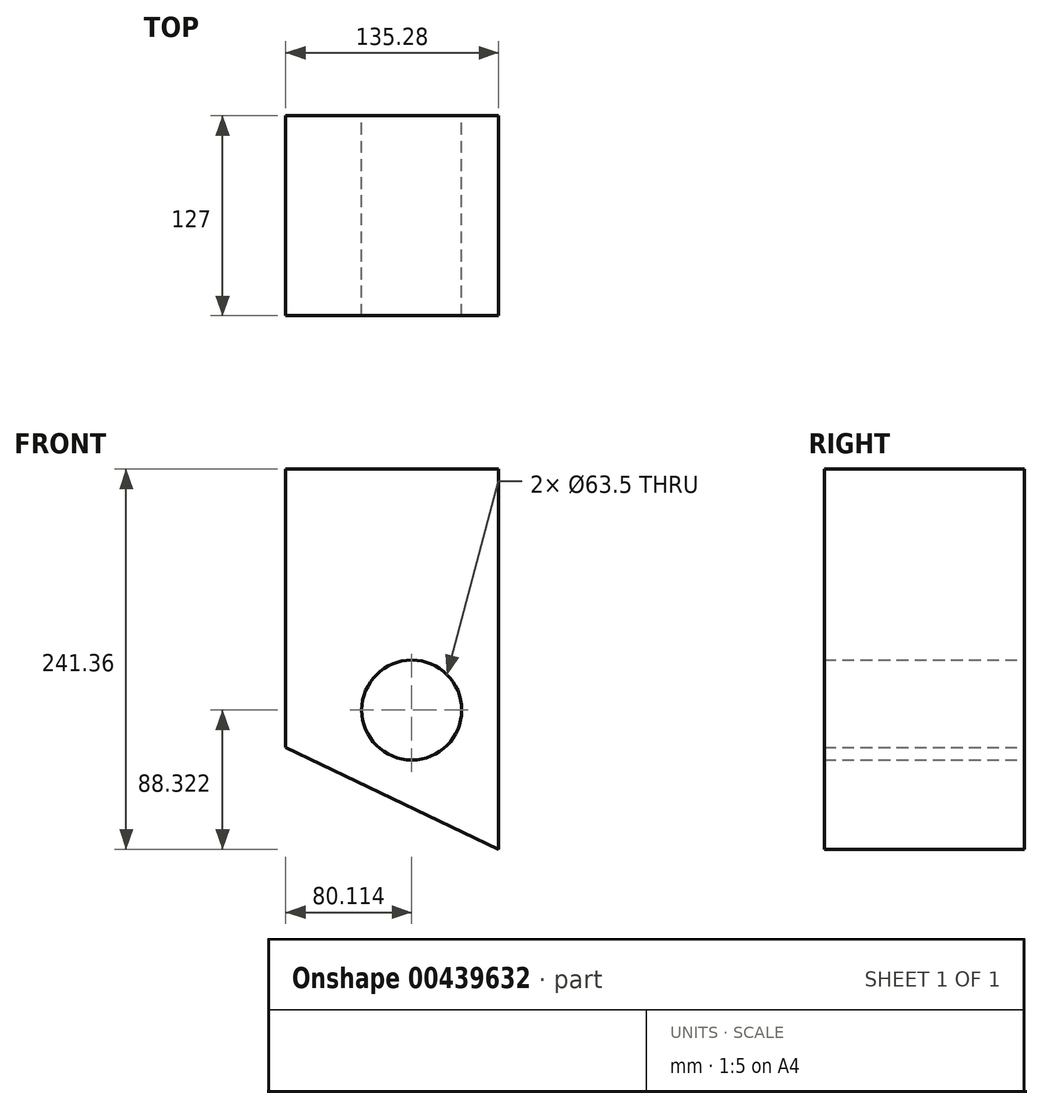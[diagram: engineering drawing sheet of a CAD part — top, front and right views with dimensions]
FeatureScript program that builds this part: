
annotation { "Feature Type Name" : "Feature", "Feature Type Description" : "" }
export const myFeature = defineFeature(function(context is Context, id is Id, definition is map)
    precondition{}
    {
        {
            var Q0;
            Q0=qCreatedBy(makeId("Front.planeOp"),FACE);
            var sketch = newSketch(context, id + "F0", { "sketchPlane" : qUnion([Q0])});
            skLineSegment(sketch, "E0", {"start": v(-120.22, -107.14) * mm, "end": v(-120.22, 69.53) * mm});
            skLineSegment(sketch, "E1", {"start": v(-120.22, 69.53) * mm, "end": v(15.06, 69.53) * mm});
            skLineSegment(sketch, "E2", {"start": v(15.06, 69.53) * mm, "end": v(15.06, -171.83) * mm});
            skLineSegment(sketch, "E3", {"start": v(-120.22, -107.14) * mm, "end": v(15.06, -171.83) * mm});
            skCircle(sketch, "E4", {"center": v(-40.1, -83.5) * mm, "radius": 31.75 * mm});
            skSolve(sketch);
        }
        {
            var Q0;
            Q0 = qSketchRegion(id + "F0", true);
            extrude(context, id + "F1", {"entities" : qUnion([Q0]), "depth" : 127 * mm});
        }
    });
